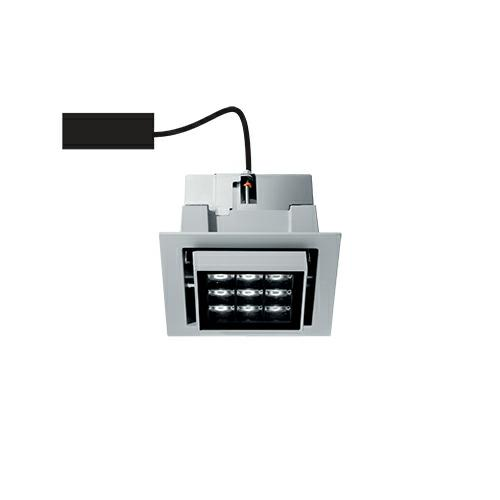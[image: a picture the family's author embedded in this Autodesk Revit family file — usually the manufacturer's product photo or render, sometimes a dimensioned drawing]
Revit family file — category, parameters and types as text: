
# Revit family: SIMES_S.7421W_Catch
name_source: partatom
category: Lighting Fixtures
revit_build: Autodesk Revit 2016 (Build: 20150714_1515(x64)
units: mm (PartAtom-declared; Revit-internal decimal feet)

## family parameters
Cut with Voids When Loaded = No
Host = Face
Light Source = Yes
OmniClass Number = 23.80.70.14
OmniClass Title = Luminaries for External Lighting
Part Type = Normal
Room Calculation Point = No
Round Connector Dimension = Use Diameter
Shared = No

## types (1)
- SIMES_S.7421W_Catch
    Approval mark = CE
    Assembly Code = D5020
    BIMobject category = Outside
    Brand url = http://www.simes.it
    Color Filter = 16777215
    Color Rendering Index = CRI 90
    Colour Temperature = 3000
    Control Gear = electronic transformer
    Default Elevation = 1219 mm
    Description = CATCH SQUARE 9LED
Art. S.7421W
MODULES LED 3000K  230V CRI 90
Rated luminaire luminous flux: 761lm
Rated input power: 15W
Luminaire efficacy: 51lm/W
Electronic ballast 220V240V 50/60Hz
CE

PRODUCT TYPE
False ceiling-recessed down-light fitting. IP rating IP 65
MATERIAL CHARACTERISTICS
Aluminium die cast housing in EN AB-47100 (low copper content) with high resistance against corrosion. Stone wash surface treatment prior to painting process. Aluminium front trim or Marine grade stainless steel AISI 316L front trim. A4 grade Stainless Steel screws with 2,5-3% molybdenum content which increases the resistance against corrosion. Pre treated Silicone Gaskets. Painting Process : 3 Step Process
1) Surface treatment with BONDERITE. A heavy metal free chemical surface treatment containing ceramic nano particles giving a cohesive, inorganic and highly dense protective coating. 2) PRE POLYMERIZATION a process of introducing an epoxy primer with excellent characteristics to the paint which also offers very high resistance to oxidation due to its Zinc content. 3) POLYMERIZATION a process with the application of polyester powder with high resistance against UV rays and harsh weather conditions. Resistance test protection for Marine applications for 1200h.  Mechanical resistance IK 08
LIGHTING PERFORMANCE
Toughened  transparent  glass 5mm thick. Lamp  adjustable ±20° position. LOR -- 
INSTALLATION AND MANTEINANCE
The luminaires are fixed to the falseceiling by a heavy-duty bracket system, adjustable from inside the luminaire. 
WIRING
Electronic circuit 220V/230V 50/60Hz in power supply box. Luminaire hard wired with 0.4m H05RN-F cable. Isolation: CLASS II . Available colours: Aluminium grey (cod.14). Weight:  Kg Glow Wire test: --
Lamp included.
REGISTERED DESIGN
This luminaire contains built-in LED modules with energy class: A, A+, A++. In case of damage or malfunction please contact the manufacturer to receive additional instructions on how to replace and relative spare parts to order. The LED modules cannot be handled in the luminaire by the end user (Regulation UE 874/2012).
LED circuit boards are engineered accordingly to actual Lumen Maintenance regulation (LM80) and Technical Memorandum (TM21) where uniformity and quality of light is 50.000 hours referred to L70  B20 Ta 25°C.Lifecycle refers to LED circuit boards only, all others components of the luminaire are excluded.
    Design country = Italy
    Dimming Lamp Color Temperature Shift = <None>
    Edition number = 1
    Frequency = 50/60Hz
    IFC Classification = Light Fixture
    IK Rating = IK 08
    Installation instructions = http://www.simes.it
    Lamp = LED
    Lamp Light Flux = 1390
    Lamp Power = 24,299999237060547
    Lamp count = 1
    Last Update = 02/08/2018 10:01:30
    Lifetime = 50000 L70 B20 Ta 25°C
    Light Output Ratio = 100
    Luminous efficacy = 50,7
    Manufacturer = SIMES
    Manufacturer country = Italy
    Manufacturer name = Simes
    Masterformat 2014 Code = 26 56 00
    Masterformat 2014 Description = Exterior Lighting
    Material main = Aluminium
    Material secondary = Glass
    Model = S.7421W
    Mounting Place = Ceiling
    Mounting Type = Recessed
    NBS Reference Code = 49
    NBS Reference Description = Luminaries And Lamps
    Nominal height = 0
    Nominal width = 0
    OmniClass Code = 23-35 47 11
    OmniClass Description = Lighting Fixture
    Photometric Web File = S7421W.ies
    Product Group = recessed luminaire
    Product Guid = 284f1ae0-b9ad-458c-8829-59ff5cf93d3c
    Product Name = Catch
    Product SKU = CATCH
    Product certification = http://www.simes.it
    Product data url = https://bimobject.com
    Product url = http://www.simes.it
    Protection Class = Protection class II
    Protection Degree = IP 65
    QR code = http://bimobject.com
    System Light Flux = 761
    System Power = 15
    Technical description = http://www.simes.it
    Tilt Angle = -90.00°
    Type Comments = SIMES S.p.A. - All rights reserved
    Type Image = catch-quad-9LED-bas_14.jpg
    UNSPSC Code = 3911
    URL = http://www.simes.it
    Uniclass 1.4 Code = YJ73
    Uniclass 1.4 Description = Luminaries and lamps
    Uniclass 2.0 Code = PR-49
    Uniclass 2.0 Description = Luminaries and lamps
    Uniclass 2015 Code = EF_70_80
    Uniclass 2015 Name = Lighting
    Uniformat II Code = D5020
    Uniformat II Description = Lighting & Branch Wiring
    Voltage = 220V240V
    Wattage Comments = 27.0W
    Weight Net (Kg) = 0

## geometry (parser evidence)
native form markers: Blend x4
no freeform markers — native parametric forms only
